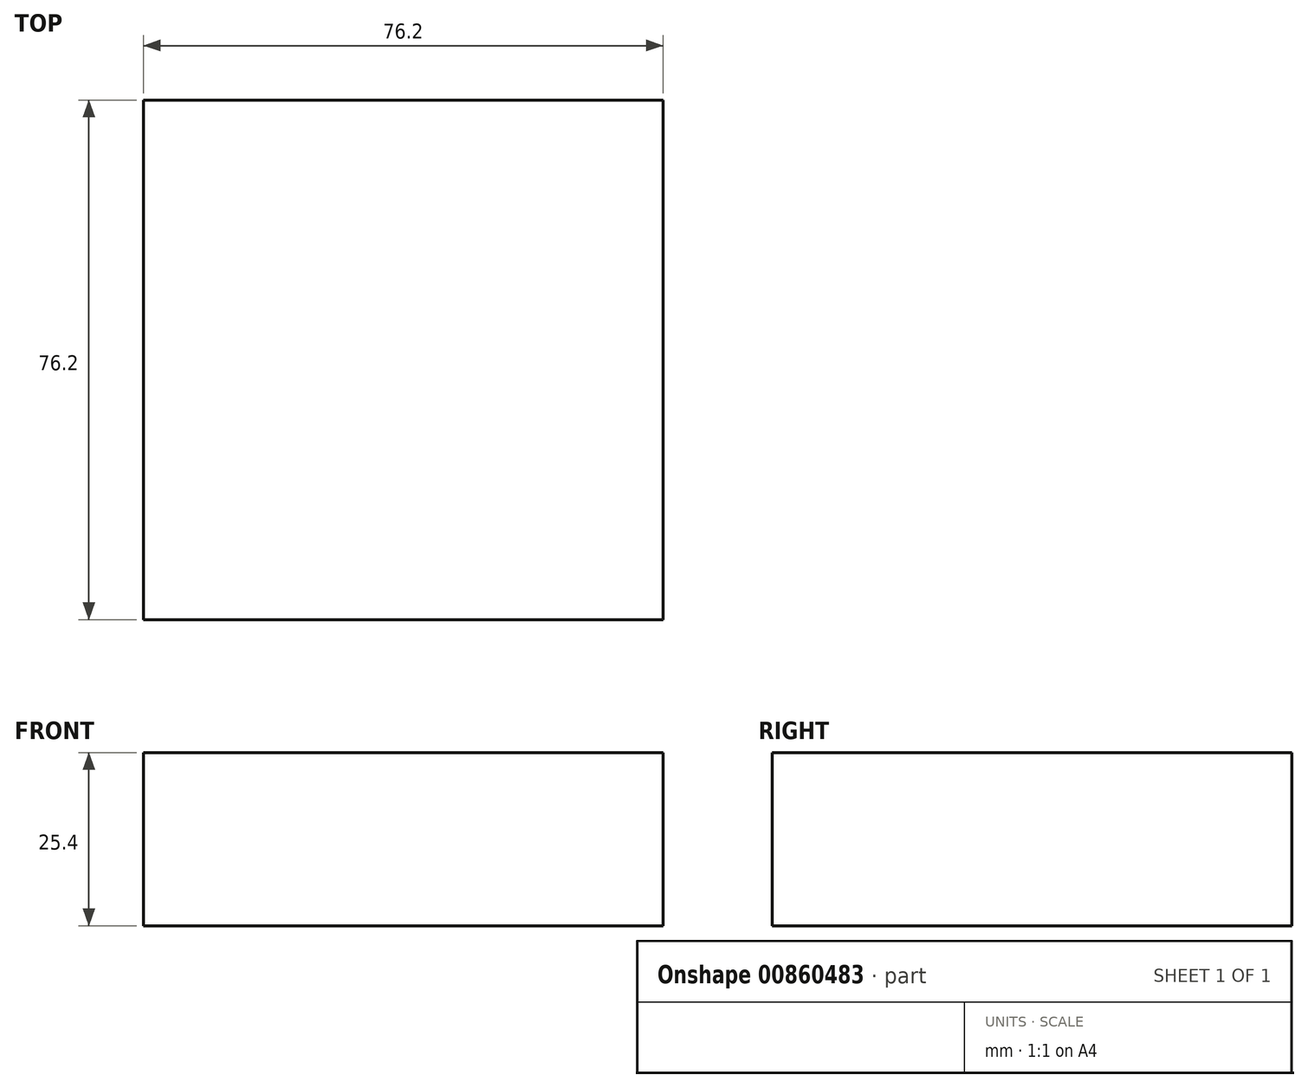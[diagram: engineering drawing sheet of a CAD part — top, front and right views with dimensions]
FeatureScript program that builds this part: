
annotation { "Feature Type Name" : "Feature", "Feature Type Description" : "" }
export const myFeature = defineFeature(function(context is Context, id is Id, definition is map)
    precondition{}
    {
        {
            var Q0;
            Q0=qCreatedBy(makeId("Top.planeOp"),FACE);
            var sketch = newSketch(context, id + "F0", { "sketchPlane" : qUnion([Q0])});
            skLineSegment(sketch, "E0.bottom", {"start": v(38.1, 38.1) * mm, "end": v(-38.1, 38.1) * mm});
            skLineSegment(sketch, "E0.top", {"start": v(38.1, -38.1) * mm, "end": v(-38.1, -38.1) * mm});
            skLineSegment(sketch, "E0.left", {"start": v(38.1, 38.1) * mm, "end": v(38.1, -38.1) * mm});
            skLineSegment(sketch, "E0.right", {"start": v(-38.1, 38.1) * mm, "end": v(-38.1, -38.1) * mm});
            skPoint(sketch, "E0.middle", {"position": v(0, 0) * mm});
            skSolve(sketch);
        }
        {
            var Q0;
            Q0=makeQuery(id+"F0.imprint","IMPRINT",FACE,{"disambiguationData":[TD([[makeQuery(id+"F0.imprint","IMPRINT",EDGE,{"derivedFrom":sQuery(id+"F0.wireOp",EDGE,"E0.bottom")}),1.0]])]});
            extrude(context, id + "F1", {"entities" : qUnion([Q0]), "depth" : 25.4 * mm, "offsetDistance" : 25.4 * mm});
        }
    });
